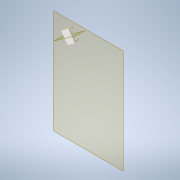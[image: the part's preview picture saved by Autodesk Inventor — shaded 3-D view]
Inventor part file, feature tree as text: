
AUTODESK INVENTOR PART (.ipt)
format: ipt  version: 2022 (Build 260153000, 153)  size: 184,320 bytes
history: native  units: mm
features: reference x6, extrude x3, sketch x3, other x3, plane x2, chamfer x1, mirror x1, projected_geometry x1
ambient origin geometry x8: Origin, YZ Plane, XZ Plane, XY Plane, X Axis, Y Axis, Z Axis, Center Point
bodies: Volumenkörper1 (feature_tree)
feature tree (20):
  plane  "Arbeitsebene1"
  extrude  "Extrusion1"  Depth=15.0mm
  extrude  "Extrusion2"  Depth=2.0mm
  chamfer  "Fase1"  Distance=2.0mm
  plane  "Arbeitsebene2"
  mirror  "Spiegeln1"
  extrude  "Extrusion3"  TaperAngle=0.0deg  [1 undecoded]
  sketch  "Skizze1"  dims[d0=21.816616mm d1=15.0mm]
  reference  "Referenz1"
  reference  "Referenz2"
  reference  "Referenz3"
  reference  "Referenz4"
  reference  "Referenz5"
  sketch  "Skizze2"  dims[d2=12.0mm d3=9.0mm d4=2.0mm d5=0.0mm]
  projected_geometry  "Projizierte Kontur1"
  reference  "Referenz6"
  sketch  "Skizze3"  dims[d6=1.5mm d7=0.0mm d8=1.0mm d9=0.3mm d10=2.0mm d11=2.0mm d12=0.0mm d13=2.0mm d14=2.0mm d15=45.0deg d16=7.9mm d17=0.0mm d18=0.0mm d19=3.2mm d20=3.2mm]
  other  "Omniscope_new_v0.iam"
  other  "OV_Camera:1"
  other  "Omniscope_mid_level_v0:1"
note: 1 required parameter value undecoded (feature->parameter linkage not recoverable at this tier; creation-order binding heuristic only, values carry confidence <= 0.55)
